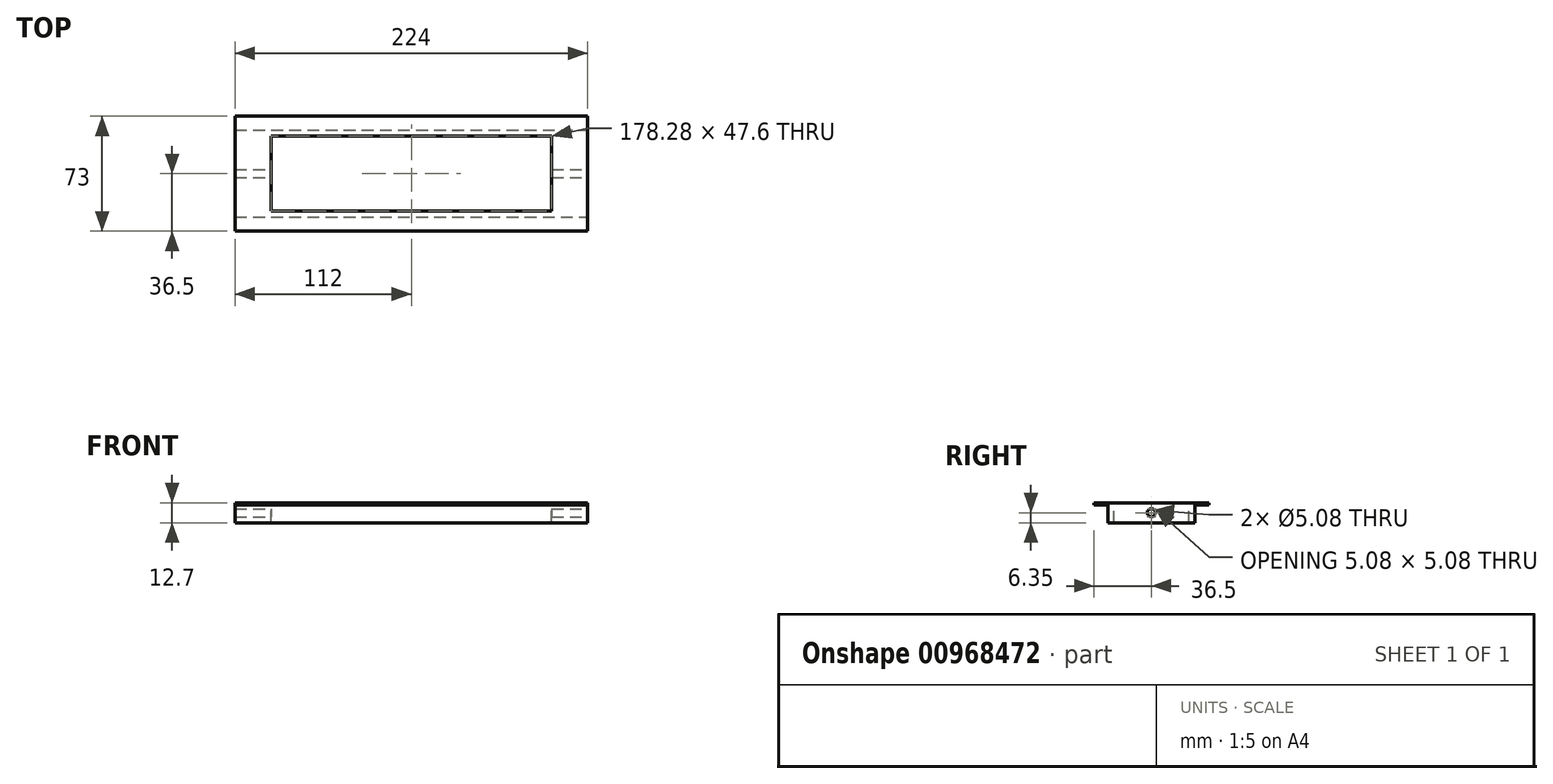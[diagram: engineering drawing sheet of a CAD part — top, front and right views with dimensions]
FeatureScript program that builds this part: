
annotation { "Feature Type Name" : "Feature", "Feature Type Description" : "" }
export const myFeature = defineFeature(function(context is Context, id is Id, definition is map)
    precondition{}
    {
        {
            var Q0;
            Q0=qCreatedBy(makeId("Top.planeOp"),FACE);
            var sketch = newSketch(context, id + "F0", { "sketchPlane" : qUnion([Q0])});
            skLineSegment(sketch, "E0.bottom", {"start": v(-112, 36.5) * mm, "end": v(112, 36.5) * mm});
            skLineSegment(sketch, "E0.top", {"start": v(-112, -36.5) * mm, "end": v(112, -36.5) * mm});
            skLineSegment(sketch, "E0.left", {"start": v(-112, 36.5) * mm, "end": v(-112, -36.5) * mm});
            skLineSegment(sketch, "E0.right", {"start": v(112, 36.5) * mm, "end": v(112, -36.5) * mm});
            skPoint(sketch, "E0.middle", {"position": v(0, 0) * mm});
            skSolve(sketch);
        }
        {
            var Q0;
            Q0=makeQuery(id+"F0.imprint","IMPRINT",FACE,{"disambiguationData":[TD([[makeQuery(id+"F0.imprint","IMPRINT",EDGE,{"derivedFrom":sQuery(id+"F0.wireOp",EDGE,"E0.bottom")}),-1.0]])]});
            extrude(context, id + "F1", {"entities" : qUnion([Q0]), "depth" : 12.7 * mm, "offsetDistance" : 25.4 * mm});
        }
        {
            var Q0;
            Q0=makeQuery(id+"F1.opExtrude","CAP_FACE",FACE,{"disambiguationData":[OSD([sQuery(id+"F0.wireOp",EDGE,"E0.bottom"),sQuery(id+"F0.wireOp",EDGE,"E0.top"),sQuery(id+"F0.wireOp",EDGE,"E0.left"),sQuery(id+"F0.wireOp",EDGE,"E0.right")])],"isStart":false});
            var sketch = newSketch(context, id + "F2", { "sketchPlane" : qUnion([Q0])});
            skLineSegment(sketch, "E1.bottom", {"start": v(-86.6, 11.1) * mm, "end": v(86.6, 11.1) * mm});
            skLineSegment(sketch, "E1.top", {"start": v(-86.6, -11.1) * mm, "end": v(86.6, -11.1) * mm});
            skLineSegment(sketch, "E1.left", {"start": v(-86.6, 11.1) * mm, "end": v(-86.6, -11.1) * mm});
            skLineSegment(sketch, "E1.right", {"start": v(86.6, 11.1) * mm, "end": v(86.6, -11.1) * mm});
            skPoint(sketch, "E1.middle", {"position": v(0, 0) * mm});
            skLineSegment(sketch, "E2.bottom", {"start": v(-89.14, 23.8) * mm, "end": v(89.14, 23.8) * mm});
            skLineSegment(sketch, "E2.top", {"start": v(-89.14, -23.8) * mm, "end": v(89.14, -23.8) * mm});
            skLineSegment(sketch, "E2.left", {"start": v(-89.14, 23.8) * mm, "end": v(-89.14, -23.8) * mm});
            skLineSegment(sketch, "E2.right", {"start": v(89.14, 23.8) * mm, "end": v(89.14, -23.8) * mm});
            skSolve(sketch);
        }
        {
            var Q0;
            Q0=makeQuery(id+"F2.imprint","IMPRINT",FACE,{"disambiguationData":[TD([[makeQuery(id+"F2.imprint","IMPRINT",EDGE,{"derivedFrom":sQuery(id+"F2.wireOp",EDGE,"E1.bottom")}),1.0]])]});
            var Q1;
            Q1=makeQuery(id+"F2.imprint","IMPRINT",FACE,{"disambiguationData":[TD([[makeQuery(id+"F2.imprint","IMPRINT",EDGE,{"derivedFrom":sQuery(id+"F2.wireOp",EDGE,"E1.bottom")}),-1.0]])]});
            extrude(context, id + "F3", {"entities" : qUnion([Q0, Q1]), "operationType" : NewBodyOperationType.REMOVE, "oppositeDirection" : true, "depth" : 25.4 * mm, "offsetDistance" : 25.4 * mm});
        }
        {
            var Q0;
            Q0=makeQuery(id+"F1.opExtrude","SWEPT_FACE",FACE,{"disambiguationData":[OSD([sQuery(id+"F0.wireOp",EDGE,"E0.right")])]});
            var sketch = newSketch(context, id + "F4", { "sketchPlane" : qUnion([Q0])});
            skLineSegment(sketch, "E3.bottom", {"start": v(-36.5, 0) * mm, "end": v(-27.6, 0) * mm});
            skLineSegment(sketch, "E3.top", {"start": v(-36.5, 11.43) * mm, "end": v(-27.6, 11.43) * mm});
            skLineSegment(sketch, "E3.left", {"start": v(-36.5, 0) * mm, "end": v(-36.5, 11.43) * mm});
            skLineSegment(sketch, "E3.right", {"start": v(-27.6, 0) * mm, "end": v(-27.6, 11.43) * mm});
            skSolve(sketch);
        }
        {
            var Q0;
            Q0=makeQuery(id+"F4.imprint","IMPRINT",FACE,{"disambiguationData":[TD([[makeQuery(id+"F4.imprint","IMPRINT",EDGE,{"derivedFrom":sQuery(id+"F4.wireOp",EDGE,"E3.bottom")}),-1.0]])]});
            extrude(context, id + "F5", {"entities" : qUnion([Q0]), "operationType" : NewBodyOperationType.REMOVE, "oppositeDirection" : true, "depth" : 508 * mm, "offsetDistance" : 25.4 * mm});
        }
        {
            var Q0;
            Q0=makeQuery(id+"F1.opExtrude","SWEPT_FACE",FACE,{"disambiguationData":[OSD([sQuery(id+"F0.wireOp",EDGE,"E0.right")])]});
            var sketch = newSketch(context, id + "F6", { "sketchPlane" : qUnion([Q0])});
            skLineSegment(sketch, "E4.bottom", {"start": v(36.5, 0) * mm, "end": v(27.6, 0) * mm});
            skLineSegment(sketch, "E4.top", {"start": v(36.5, 11.43) * mm, "end": v(27.6, 11.43) * mm});
            skLineSegment(sketch, "E4.left", {"start": v(36.5, 0) * mm, "end": v(36.5, 11.43) * mm});
            skLineSegment(sketch, "E4.right", {"start": v(27.6, 0) * mm, "end": v(27.6, 11.43) * mm});
            skSolve(sketch);
        }
        {
            var Q0;
            Q0=makeQuery(id+"F6.imprint","IMPRINT",FACE,{"disambiguationData":[TD([[makeQuery(id+"F6.imprint","IMPRINT",EDGE,{"derivedFrom":sQuery(id+"F6.wireOp",EDGE,"E4.bottom")}),-1.0]])]});
            extrude(context, id + "F7", {"entities" : qUnion([Q0]), "operationType" : NewBodyOperationType.REMOVE, "oppositeDirection" : true, "depth" : 508 * mm, "offsetDistance" : 25.4 * mm});
        }
        {
            var Q0;
            Q0=makeQuery(id+"F1.opExtrude","SWEPT_FACE",FACE,{"disambiguationData":[OSD([sQuery(id+"F0.wireOp",EDGE,"E0.right")])]});
            var sketch = newSketch(context, id + "F8", { "sketchPlane" : qUnion([Q0])});
            skCircle(sketch, "E5", {"center": v(0, 6.35) * mm, "radius": 2.54 * mm});
            skPoint(sketch, "E5.centerSnap0", {"position": v(0, 0) * mm});
            skSolve(sketch);
        }
        {
            var Q0;
            Q0=makeQuery(id+"F8.imprint","IMPRINT",FACE,{"disambiguationData":[TD([[makeQuery(id+"F8.imprint","IMPRINT",EDGE,{"derivedFrom":sQuery(id+"F8.wireOp",EDGE,"E5")}),1.0]])]});
            extrude(context, id + "F9", {"entities" : qUnion([Q0]), "operationType" : NewBodyOperationType.REMOVE, "oppositeDirection" : true, "depth" : 508 * mm, "offsetDistance" : 25.4 * mm});
        }
    });
